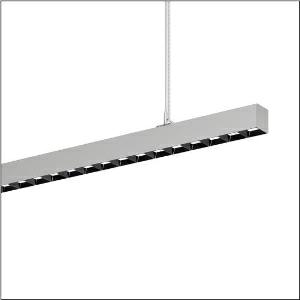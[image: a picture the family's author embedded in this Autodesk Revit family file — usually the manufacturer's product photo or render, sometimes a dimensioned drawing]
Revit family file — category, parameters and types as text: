
# Revit family: silica_r__21_51mx32tctds_853f
name_source: partatom
category: Lighting Fixtures
units: mm (PartAtom-declared; Revit-internal decimal feet)

## family parameters
Cut with Voids When Loaded = No
Host = Face
Light Source = No
Part Type = Normal
Room Calculation Point = No
Round Connector Dimension = Use Diameter
Shared = No

## types (1)
- --- (1 x LED, 15540 lm, 133.6 W, 6500K)
    Apparent Load = 134 VA
    CIE Flux Codes = 84 99 100 60 100
    Color Rendering = 80
    Color Temperature = 6500K
    Default Elevation = 1800 mm
    Description = Silica® 21, office luminaire, primary light control with darklight reflector, of PMMA, black, CAT 2 (L<= 3000cd/m²), light emission: direct/indirect distribution, primary light characteristic: symmetric, installation type: suspended mounting, LED, rated luminous flux: 15.540lm, luminous efficacy: 111lm/W, light colour: 8tw, colour temperature: 2700..6500K, control gear: ECG DALI, with terminal, 3+2-pole, max. 2.5mm², mains connection: 220..240V, AC, 50/60Hz, rated input power: 140.3W, luminaire housing, of aluminium, metallic grey (RAL 9006), length: 3.004mm, width: 53mm, height: 53mm, protection rating (complete): IP20, insulation class (complete): insulation class I (protective earthing), certification: CE, permissible operating ambient temperature: 0..+35°C, standard: EN 50419, packaging unit: 1 piece
    Height = 53 mm
    Lamp = 1 x LED
    Lamp Light Flux = 15540 lm
    Lamp Power = 133.6 W
    Lamp count = 1
    Length = 3004 mm
    Luminous efficacy = 116 lm/W
    Manufacturer = Siteco
    ModVariant = No
    Model = 51MX32TCTDS
    Mounting Place = Ceiling
    Mounting Type = Pendant
    Number of Poles = 1
    OnlyDefault = Yes
    Power Factor = 1
    Product Name = Silica® 21
    Product group = office luminaire | ceiling pendant
    ProductGroupID = 902
    Protection Class = Protection class I
    Protection Degree = IP 20
    RLX_Detail_Level = 1
    RLX_Emergency_Light_Flux = 0 lm
    RLX_Emergency_Type = 0
    RLX_Emergency_Type_DB = No
    RlxData = <blob elided: 61933 chars, md5=fe59fcff>
    Socket = socket
    Standby Power = 0 W
    System Light Flux = 15540 lm
    System Power = 134 W
    Type Comments = individual setting
    Type Image = l_1313642.jpg
    URL = http://relux.com
    VarID = @adj_089283
    Voltage = 0 V
    Weight = 0.00 kg
    Width = 53 mm

## geometry (parser evidence)
native form markers: Blend x4, Sweep x12
no freeform markers — native parametric forms only
